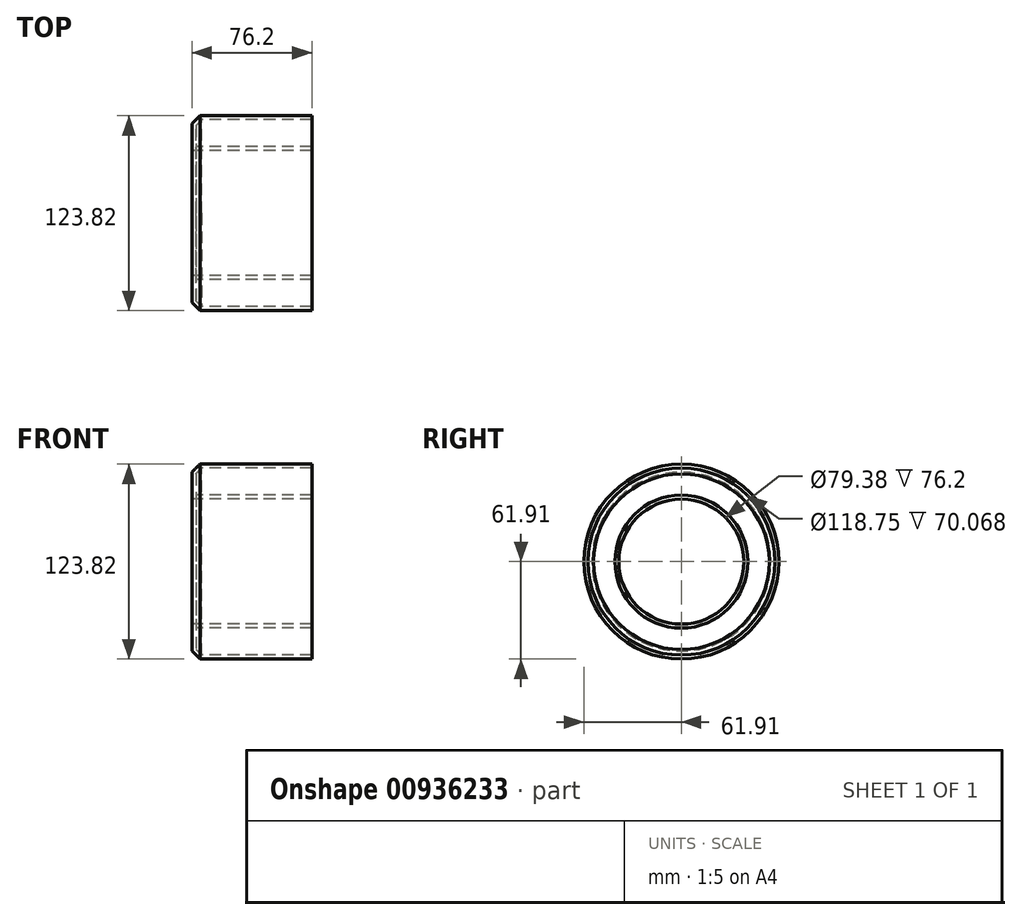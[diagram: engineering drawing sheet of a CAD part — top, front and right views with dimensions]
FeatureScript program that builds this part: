
annotation { "Feature Type Name" : "Feature", "Feature Type Description" : "" }
export const myFeature = defineFeature(function(context is Context, id is Id, definition is map)
    precondition{}
    {
        {
            var Q0;
            Q0=qCreatedBy(makeId("Front.planeOp"),FACE);
            var sketch = newSketch(context, id + "F0", { "sketchPlane" : qUnion([Q0])});
            skLineSegment(sketch, "E0.bottom", {"start": v(38.1, 39.69) * mm, "end": v(-38.1, 39.69) * mm});
            skLineSegment(sketch, "E0.top", {"start": v(38.1, 61.91) * mm, "end": v(-38.1, 61.91) * mm});
            skLineSegment(sketch, "E0.left", {"start": v(38.1, 39.69) * mm, "end": v(38.1, 61.91) * mm});
            skLineSegment(sketch, "E0.right", {"start": v(-38.1, 39.69) * mm, "end": v(-38.1, 61.91) * mm});
            skPoint(sketch, "E0.middle", {"position": v(0, 50.8) * mm});
            skLineSegment(sketch, "E1", {"start": v(-63.53, 0) * mm, "end": v(51.01, 0) * mm, "construction": true});
            skSolve(sketch);
        }
        {
            var Q0;
            Q0=makeQuery(id+"F0.imprint","IMPRINT",FACE,{"disambiguationData":[TD([[makeQuery(id+"F0.imprint","IMPRINT",EDGE,{"derivedFrom":sQuery(id+"F0.wireOp",EDGE,"E0.bottom")}),-1.0]])]});
            var Q1;
            Q1=sQuery(id+"F0.wireOp",EDGE,"E1");
            revolve(context, id + "F1", {"surfaceOperationType" : NewSurfaceOperationType.NEW, "entities" : qUnion([Q0]), "axis" : qUnion([Q1]), "revolveType" : RevolveType.FULL});
        }
        {
            var Q0;
            Q0=makeQuery(id+"F1.opRevolve","SWEPT_EDGE",EDGE,{"disambiguationData":[OSD([sQuery(id+"F0.wireOp",EDGE,"E0.top"),sQuery(id+"F0.wireOp",EDGE,"E0.right")])]});
            chamfer(context, id + "F2", {"entities" : qUnion([Q0]), "width" : 5.08 * mm, "tangentPropagation" : true});
        }
        {
            var Q0;
            Q0=makeQuery(id+"F1.opRevolve","SWEPT_FACE",FACE,{"disambiguationData":[OSD([sQuery(id+"F0.wireOp",EDGE,"E0.left")])]});
            shell(context, id + "F3", {"entities" : qUnion([Q0]), "thickness" : 2.54 * mm});
        }
    });
